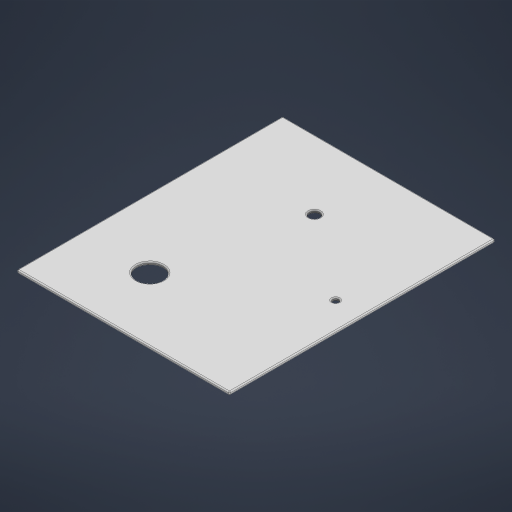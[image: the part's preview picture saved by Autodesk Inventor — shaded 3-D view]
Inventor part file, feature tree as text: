
AUTODESK INVENTOR PART (.ipt)
format: ipt  version: 2023 (Build 270158000, 158)  size: 236,032 bytes
history: native  units: mm
features: extrude x1, fillet x1, other x1
ambient origin geometry x8: Origin, YZ Plane, XZ Plane, XY Plane, X Axis, Y Axis, Z Axis, Center Point
bodies: Solid1 (feature_tree)
feature tree (3):
  extrude  "not"  Depth=200.0mm
  fillet  "Fillet1"  Radius=250.0mm
  other  "page_lines"
